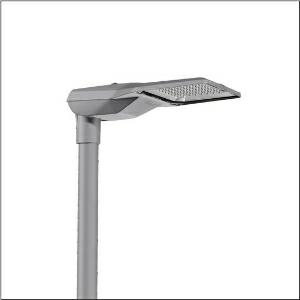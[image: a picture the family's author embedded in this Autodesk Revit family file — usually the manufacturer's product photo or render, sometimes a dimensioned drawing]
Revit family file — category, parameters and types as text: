
# Revit family: streetlight_sl_21_midi___stw1_0a_5xe3e33s08nb_8a4c
name_source: partatom
category: Lighting Fixtures
units: mm (PartAtom-declared; Revit-internal decimal feet)

## family parameters
Cut with Voids When Loaded = No
Host = Face
Light Source = No
Part Type = Normal
Room Calculation Point = No
Round Connector Dimension = Use Diameter
Shared = No

## types (1)
- --- (1 x LED, 22700 lm, 151.2 W, 3000K)
    Apparent Load = 151 VA
    CIE Flux Codes = 39 75 98 100 100
    Color Rendering = 70
    Color Temperature = 3000K
    Default Elevation = 1800 mm
    Description = Streetlight SL 21 midi, mast luminaire, primary light control with lens, of PMMA, primary optical cover: cover, of toughened safety glass, transparent, light distribution: STW1.0a, light emission: direct distribution, primary light characteristic: asymmetric, installation type: side-entry, post-top, LED, High Power LED, rated luminous flux: 22.700lm, luminous efficacy: 150lm/W, light colour: 730, colour temperature: 3000K, control gear: D4i, control: overheat protection, constant luminous flux control, time-dependent luminous flux control, flexible luminous flux parameterisation, pre-setting: logarithmic dimming characteristic, mains connection: 230..240V, AC, 50/60Hz, start of lifetime: 151W, end of service life: 157W, reduction: 70W, luminaire housing, of diecast aluminium, powder-coated, SITECO metallic grey (DB 702S), corrosivity category C5 high according to DIN EN ISO 12944, please order mast flange separately, inclination adjustable: 0°, 5°, 10°, 15°, sealing non-destructively replaceable, multi-level sealing system, length: 644mm, width: 335mm, height: 110mm, mast flange for spigot size: 42mm (side-entry): 5XC10008XM4, 60/48mm (side-entry/post-top): 5XC10108XM2, 76/60mm (side-entry/post-top): 5XC10108XM1, mounting height: 4..8m, Smart Interface above, protection rating (complete): IP66, insulation class (complete): insulation class II (safety insulation), certification: CE, ENEC, ENEC+, VDE, impact resistance: IK10, permissible operating ambient temperature for outdoor applications: -40..+50°C, standard-compliant lighting for roads and squares, packaging unit: 1 piece

Light Distribution: STW1.0a
    Height = 111 mm
    Lamp = 1 x LED
    Lamp Light Flux = 22700 lm
    Lamp Power = 151.2 W
    Lamp count = 1
    Length = 644 mm
    Luminous efficacy = 150 lm/W
    Manufacturer = Siteco
    ModVariant = No
    Model = 5XE3E33S08NB
    Number of Poles = 1
    OnlyDefault = Yes
    Power Factor = 1
    Product Name = Streetlight SL 21 midi | STW1.0a
    Product group = mast luminaire | pylon top
    ProductGroupID = 6100
    Protection Class = Protection class II
    Protection Degree = IP 66
    RLX_Detail_Level = 1
    RLX_Emergency_Light_Flux = 0 lm
    RLX_Emergency_Type = 0
    RLX_Emergency_Type_DB = No
    RlxData = <blob elided: 27005 chars, md5=4e9156ac>
    Socket = socket
    Standby Power = 0 W
    System Light Flux = 22700 lm
    System Power = 151 W
    Type Comments = factory setting: luminous flux: 100 % | dim-lin: 254 | 802 mA
    Type Image = l_1004302.jpg
    URL = http://relux.com
    VarID = @adj_169163
    Voltage = 0 V
    Weight = 0.00 kg
    Width = 336 mm

## geometry (parser evidence)
native form markers: Blend x4, Sweep x13
no freeform markers — native parametric forms only
